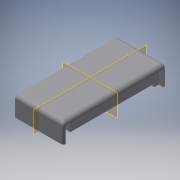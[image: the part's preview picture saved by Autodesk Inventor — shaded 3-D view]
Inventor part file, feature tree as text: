
AUTODESK INVENTOR PART (.ipt)
format: ipt  version: 2016 (Build 200138000, 138)  size: 223,744 bytes
history: native  units: mm
features: reference x7, projected_geometry x6, extrude x4, sketch x4, mirror x3, fillet x3, plane x2
ambient origin geometry x8: Origin, YZ Plane, XZ Plane, XY Plane, X Axis, Y Axis, Z Axis, Center Point
bodies: Solid1 (feature_tree)
feature tree (29):
  extrude  "Extrusion1"  Depth=3.0mm TaperAngle=0.0deg
  extrude  "Extrusion2"  Depth=3.5mm TaperAngle=0.0deg
  extrude  "Extrusion3"  Depth=1.25mm
  plane  "Work Plane1"
  plane  "Work Plane2"
  mirror  "Mirror1"
  mirror  "Mirror2"
  extrude  "Extrusion4"  Depth=1.0mm
  mirror  "Mirror3"
  fillet  "Fillet1"  Radius=3.5mm
  fillet  "Fillet3"  Radius=1.0mm
  fillet  "Fillet4"  Radius=1.0mm
  sketch  "Sketch1"  dims[d0=26.0mm d1=3.0mm d2=0.0mm]
  reference  "Reference1"
  reference  "Reference2"
  sketch  "Sketch2"  dims[d3=2.0mm d4=0.0mm d17=3.5mm d18=0.0mm]
  projected_geometry  "Projected Loop1"
  reference  "Reference3"
  sketch  "Sketch4"  dims[d19=1.125mm d20=1.25mm]
  projected_geometry  "Projected Loop3"
  projected_geometry  "Projected Loop4"
  reference  "Reference4"
  reference  "Reference5"
  reference  "Reference6"
  reference  "Reference7"
  sketch  "Sketch5"  dims[d21=1.0mm d22=1.0mm d24=3.5mm d25=0.0mm d26=1.0mm d28=1.0mm d29=0.5mm]
  projected_geometry  "Projected Loop5"
  projected_geometry  "Projected Loop6"
  projected_geometry  "Projected Loop7"
